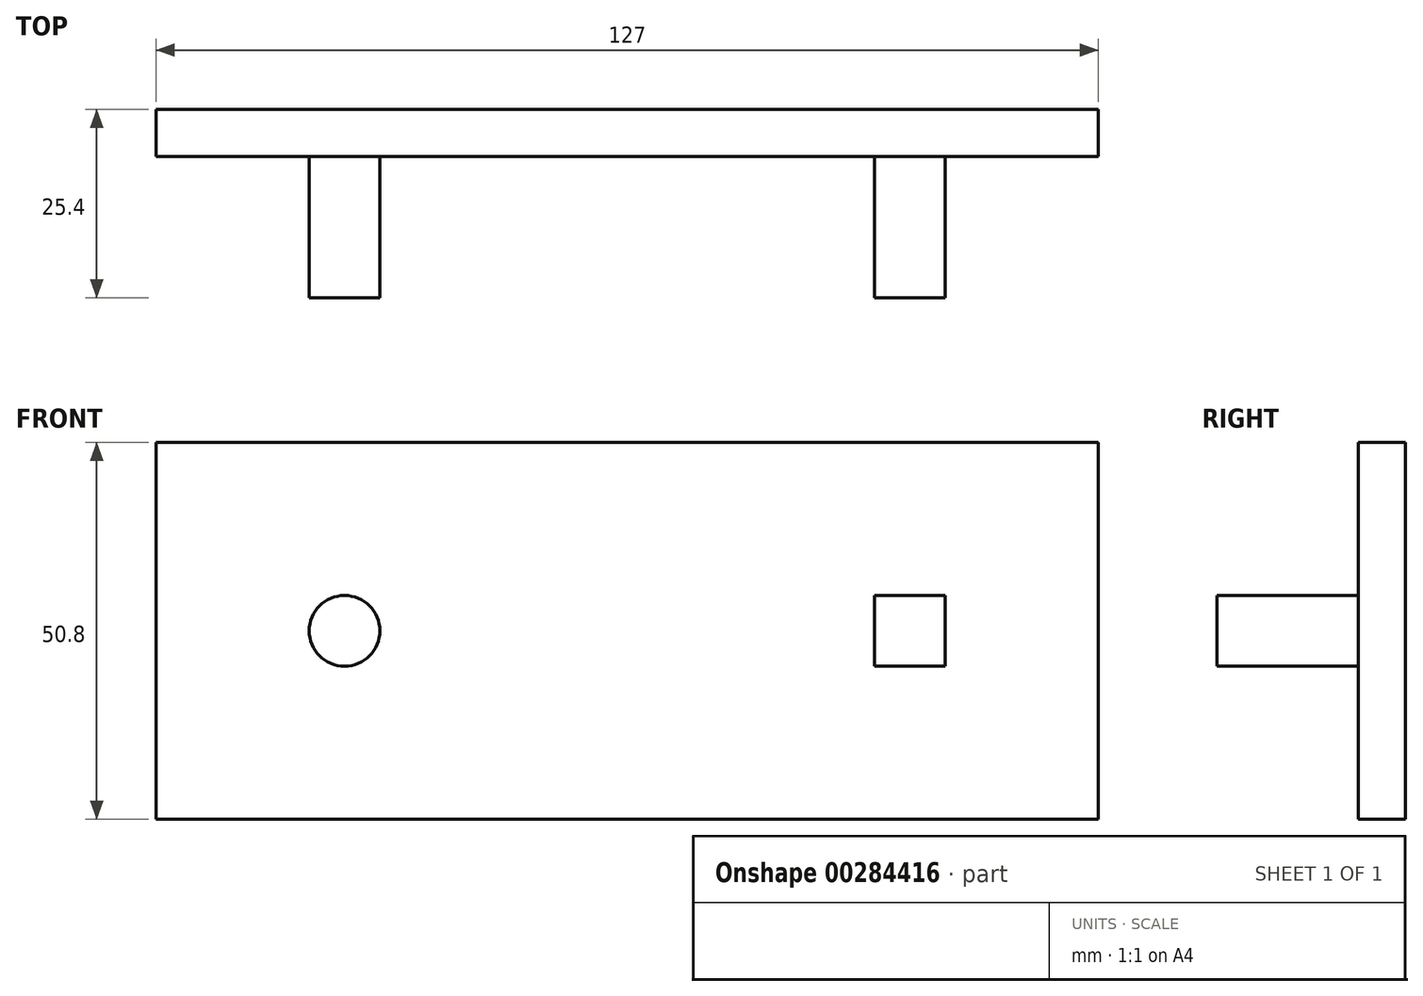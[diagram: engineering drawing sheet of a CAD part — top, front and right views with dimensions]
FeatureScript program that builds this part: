
annotation { "Feature Type Name" : "Feature", "Feature Type Description" : "" }
export const myFeature = defineFeature(function(context is Context, id is Id, definition is map)
    precondition{}
    {
        {
            var Q0;
            Q0=qCreatedBy(makeId("Front.planeOp"),FACE);
            var sketch = newSketch(context, id + "F0", { "sketchPlane" : qUnion([Q0])});
            skLineSegment(sketch, "E0.bottom", {"start": v(63.5, 25.4) * mm, "end": v(-63.5, 25.4) * mm});
            skLineSegment(sketch, "E0.top", {"start": v(63.5, -25.4) * mm, "end": v(-63.5, -25.4) * mm});
            skLineSegment(sketch, "E0.left", {"start": v(63.5, 25.4) * mm, "end": v(63.5, -25.4) * mm});
            skLineSegment(sketch, "E0.right", {"start": v(-63.5, 25.4) * mm, "end": v(-63.5, -25.4) * mm});
            skPoint(sketch, "E0.middle", {"position": v(0, 0) * mm});
            skCircle(sketch, "E1", {"center": v(-38.1, 0) * mm, "radius": 4.76 * mm});
            skLineSegment(sketch, "E2.bottom", {"start": v(42.86, -4.76) * mm, "end": v(33.34, -4.76) * mm});
            skLineSegment(sketch, "E2.top", {"start": v(42.86, 4.76) * mm, "end": v(33.34, 4.76) * mm});
            skLineSegment(sketch, "E2.left", {"start": v(42.86, -4.76) * mm, "end": v(42.86, 4.76) * mm});
            skLineSegment(sketch, "E2.right", {"start": v(33.34, -4.76) * mm, "end": v(33.34, 4.76) * mm});
            skPoint(sketch, "E2.middle", {"position": v(38.1, 0) * mm});
            skSolve(sketch);
        }
        {
            var Q0;
            Q0=makeQuery(id+"F0.imprint","IMPRINT",FACE,{"disambiguationData":[TD([[makeQuery(id+"F0.imprint","IMPRINT",EDGE,{"derivedFrom":sQuery(id+"F0.wireOp",EDGE,"E1")}),1.0]])]});
            var Q1;
            Q1=makeQuery(id+"F0.imprint","IMPRINT",FACE,{"disambiguationData":[TD([[makeQuery(id+"F0.imprint","IMPRINT",EDGE,{"derivedFrom":sQuery(id+"F0.wireOp",EDGE,"E2.bottom")}),-1.0]])]});
            var Q2;
            Q2=makeQuery(id+"F0.imprint","IMPRINT",FACE,{"disambiguationData":[TD([[makeQuery(id+"F0.imprint","IMPRINT",EDGE,{"derivedFrom":sQuery(id+"F0.wireOp",EDGE,"E0.bottom")}),1.0]])]});
            extrude(context, id + "F1", {"entities" : qUnion([Q0, Q1, Q2]), "depth" : 6.35 * mm});
        }
        {
            var Q0;
            Q0=makeQuery(id+"F0.imprint","IMPRINT",FACE,{"disambiguationData":[TD([[makeQuery(id+"F0.imprint","IMPRINT",EDGE,{"derivedFrom":sQuery(id+"F0.wireOp",EDGE,"E1")}),1.0]])]});
            var Q1;
            Q1=makeQuery(id+"F0.imprint","IMPRINT",FACE,{"disambiguationData":[TD([[makeQuery(id+"F0.imprint","IMPRINT",EDGE,{"derivedFrom":sQuery(id+"F0.wireOp",EDGE,"E2.bottom")}),-1.0]])]});
            extrude(context, id + "F2", {"entities" : qUnion([Q0, Q1]), "operationType" : NewBodyOperationType.ADD, "depth" : 25.4 * mm});
        }
    });
